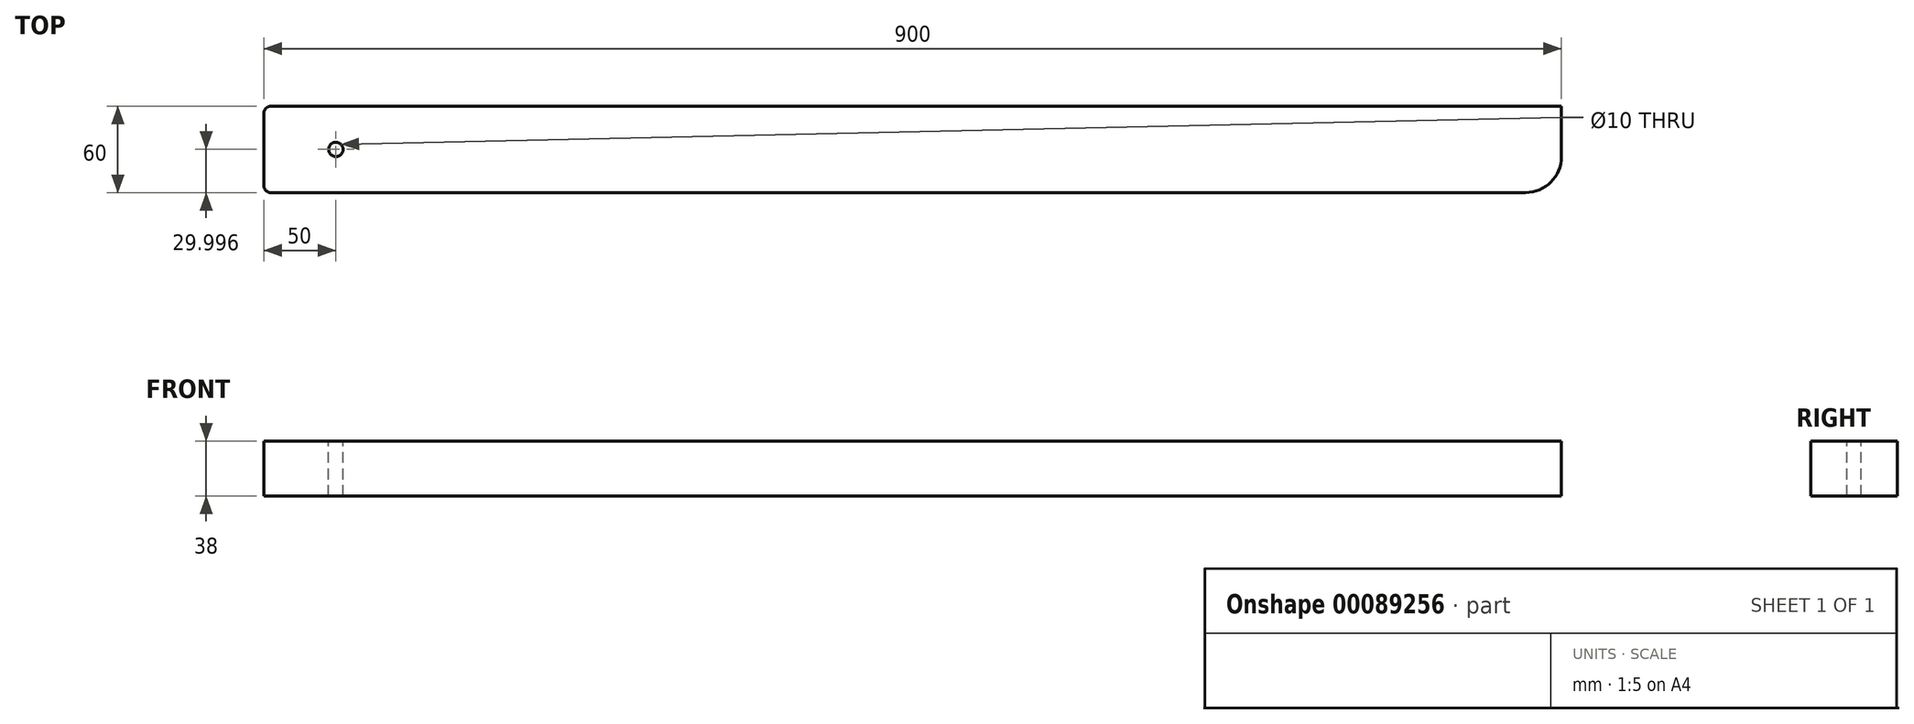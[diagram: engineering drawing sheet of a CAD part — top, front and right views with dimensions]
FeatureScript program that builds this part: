
annotation { "Feature Type Name" : "Feature", "Feature Type Description" : "" }
export const myFeature = defineFeature(function(context is Context, id is Id, definition is map)
    precondition{}
    {
        {
            var Q0;
            Q0=qCreatedBy(makeId("Right.planeOp"),FACE);
            var sketch = newSketch(context, id + "F0", { "sketchPlane" : qUnion([Q0])});
            skLineSegment(sketch, "E0.bottom", {"start": v(-35.11, 19) * mm, "end": v(24.89, 19) * mm});
            skLineSegment(sketch, "E0.top", {"start": v(-35.11, -19) * mm, "end": v(24.89, -19) * mm});
            skLineSegment(sketch, "E0.left", {"start": v(-35.11, 19) * mm, "end": v(-35.11, -19) * mm});
            skLineSegment(sketch, "E0.right", {"start": v(24.89, 19) * mm, "end": v(24.89, -19) * mm});
            skPoint(sketch, "E0.middle", {"position": v(-5.11, 0) * mm});
            skSolve(sketch);
        }
        {
            var Q0;
            Q0=makeQuery(id+"F0.imprint","IMPRINT",FACE,{"disambiguationData":[TD([[makeQuery(id+"F0.imprint","IMPRINT",EDGE,{"derivedFrom":sQuery(id+"F0.wireOp",EDGE,"E0.bottom")}),-1.0]])]});
            extrude(context, id + "F1", {"entities" : qUnion([Q0]), "depth" : 900 * mm});
        }
        {
            var Q0;
            Q0=makeQuery(id+"F1.opExtrude","CAP_EDGE",EDGE,{"disambiguationData":[OSD([sQuery(id+"F0.wireOp",EDGE,"E0.left")])],"isStart":false});
            fillet(context, id + "F2", {"entities" : qUnion([Q0]), "radius" : 25 * mm, "tangentPropagation" : true, "allowEdgeOverflow" : false});
        }
        {
            var Q0;
            Q0=makeQuery(id+"F1.opExtrude","CAP_EDGE",EDGE,{"disambiguationData":[OSD([sQuery(id+"F0.wireOp",EDGE,"E0.right")])],"isStart":true});
            var Q1;
            Q1=makeQuery(id+"F1.opExtrude","CAP_EDGE",EDGE,{"disambiguationData":[OSD([sQuery(id+"F0.wireOp",EDGE,"E0.left")])],"isStart":true});
            fillet(context, id + "F3", {"entities" : qUnion([Q0, Q1]), "radius" : 5 * mm, "tangentPropagation" : true, "allowEdgeOverflow" : false});
        }
        {
            var Q0;
            Q0=makeQuery(id+"F1.opExtrude","SWEPT_FACE",FACE,{"disambiguationData":[OSD([sQuery(id+"F0.wireOp",EDGE,"E0.bottom")])]});
            var sketch = newSketch(context, id + "F4", { "sketchPlane" : qUnion([Q0])});
            skCircle(sketch, "E1", {"center": v(50, -5.11) * mm, "radius": 5 * mm});
            skLineSegment(sketch, "E2", {"start": v(0, -5.11) * mm, "end": v(72.36, -5.11) * mm, "construction": true});
            skSolve(sketch);
        }
        {
            var Q0;
            Q0=makeQuery(id+"F4.imprint","IMPRINT",FACE,{"disambiguationData":[TD([[makeQuery(id+"F4.imprint","IMPRINT",EDGE,{"derivedFrom":sQuery(id+"F4.wireOp",EDGE,"E1")}),1.0]])]});
            extrude(context, id + "F5", {"entities" : qUnion([Q0]), "operationType" : NewBodyOperationType.REMOVE, "endBound" : BoundingType.THROUGH_ALL, "oppositeDirection" : true, "depth" : 25 * mm});
        }
    });
